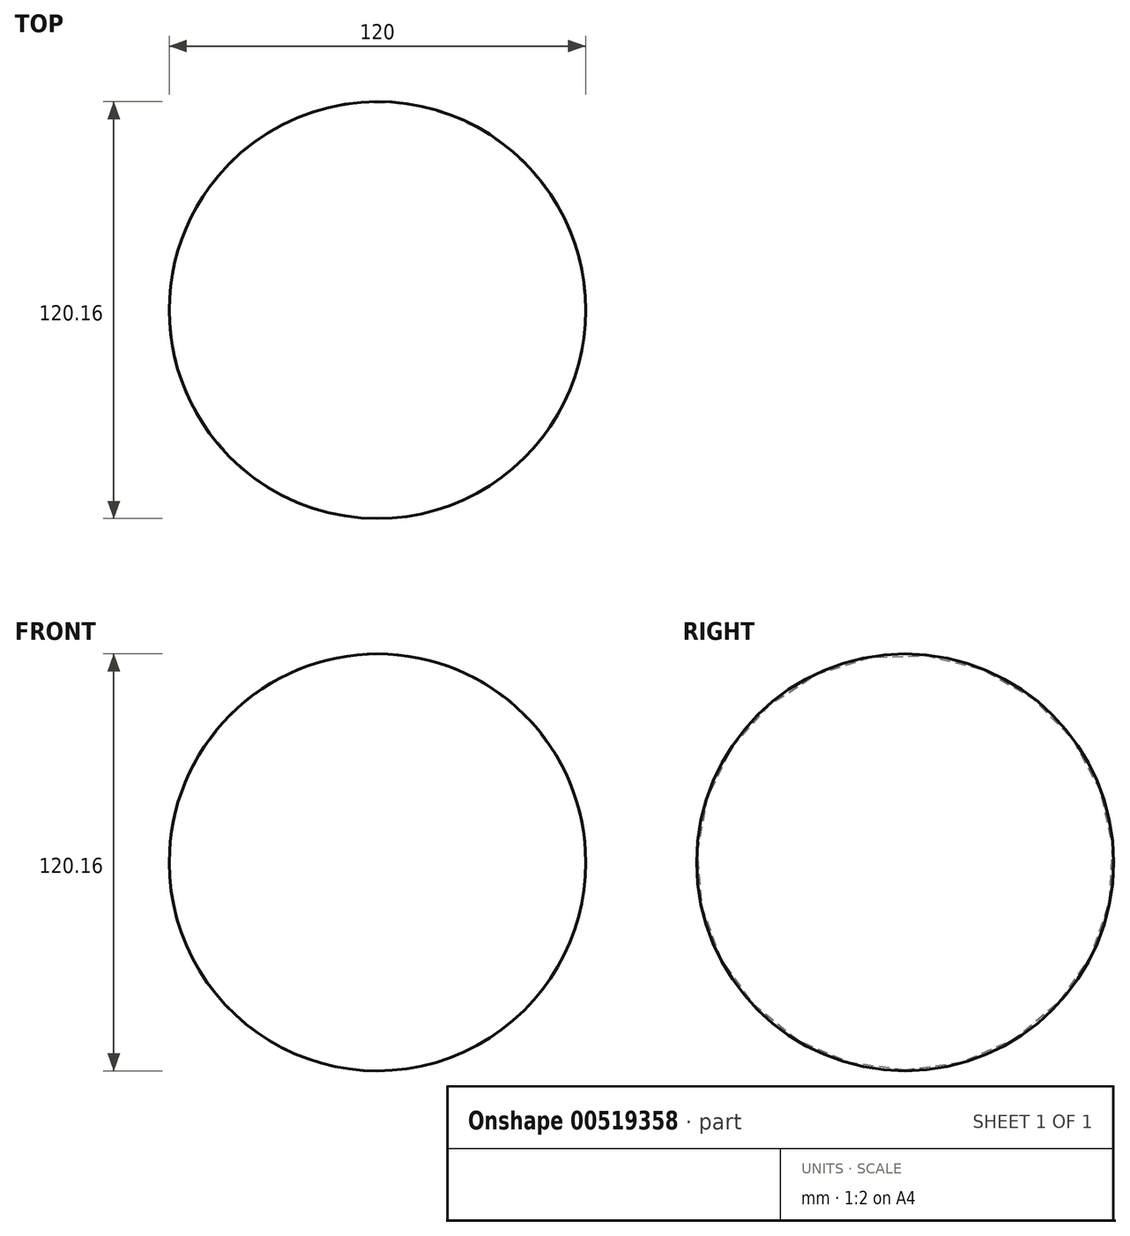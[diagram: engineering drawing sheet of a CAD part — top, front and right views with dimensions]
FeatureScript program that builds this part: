
annotation { "Feature Type Name" : "Feature", "Feature Type Description" : "" }
export const myFeature = defineFeature(function(context is Context, id is Id, definition is map)
    precondition{}
    {
        {
            var Q0;
            Q0=qCreatedBy(makeId("Front.planeOp"),FACE);
            var sketch = newSketch(context, id + "F0", { "sketchPlane" : qUnion([Q0])});
            skArc(sketch, "E0", {"start": v(59.03, 0) * mm, "mid": v(-0.97, 59.92) * mm, "end": v(-60.97, 0) * mm});
            skLineSegment(sketch, "E1", {"start": v(-60.97, 0) * mm, "end": v(59.03, 0) * mm});
            skSolve(sketch);
        }
        {
            var Q0;
            Q0=makeQuery(id+"F0.imprint","IMPRINT",FACE,{"disambiguationData":[TD([[makeQuery(id+"F0.imprint","IMPRINT",EDGE,{"derivedFrom":sQuery(id+"F0.wireOp",EDGE,"E0")}),1.0]])]});
            var Q1;
            Q1=sQuery(id+"F0.wireOp",EDGE,"E1");
            revolve(context, id + "F1", {"entities" : qUnion([Q0]), "axis" : qUnion([Q1]), "revolveType" : RevolveType.FULL});
        }
    });
